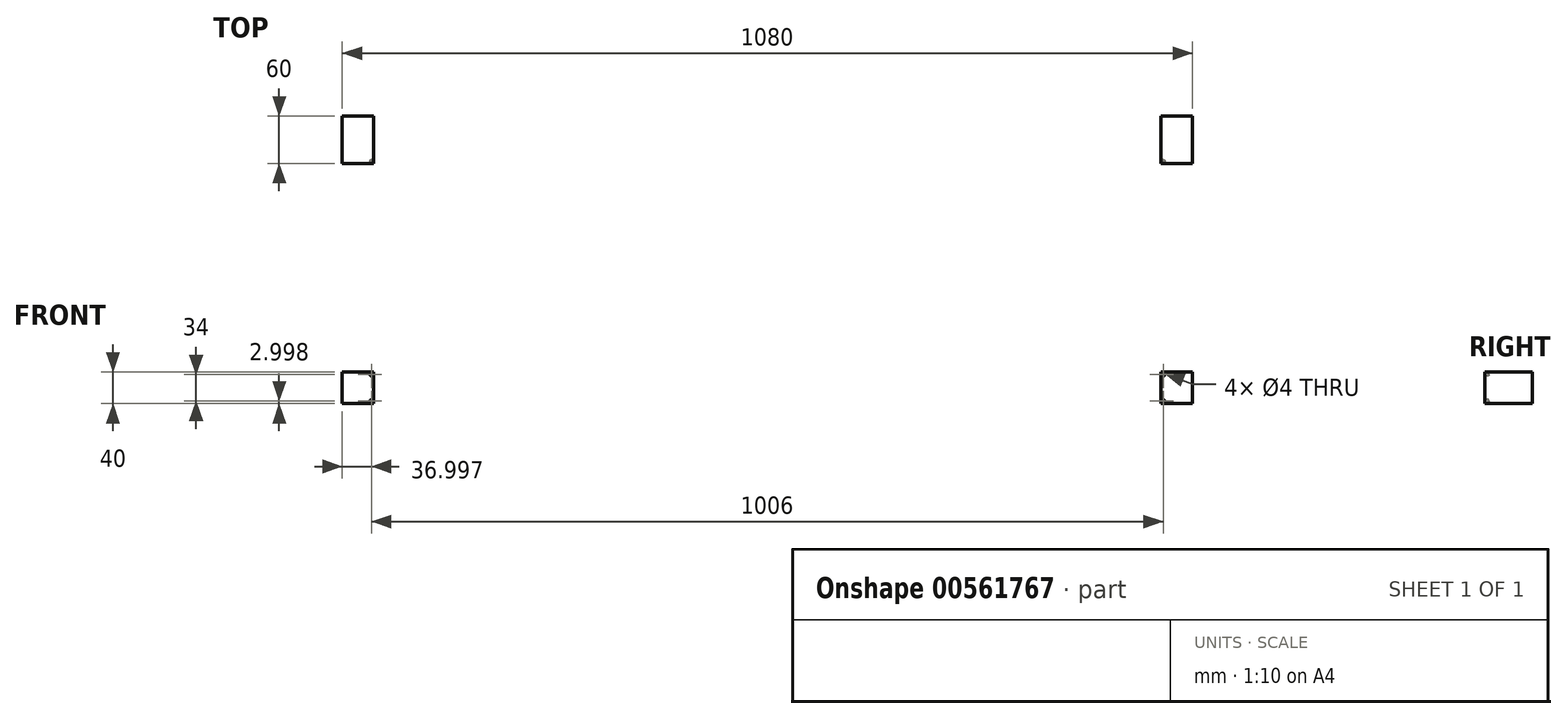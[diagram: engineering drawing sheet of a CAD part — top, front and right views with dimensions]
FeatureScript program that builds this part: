
annotation { "Feature Type Name" : "Feature", "Feature Type Description" : "" }
export const myFeature = defineFeature(function(context is Context, id is Id, definition is map)
    precondition{}
    {
        {
            var Q0;
            Q0=qCreatedBy(makeId("Front.planeOp"),FACE);
            var sketch = newSketch(context, id + "F0", { "sketchPlane" : qUnion([Q0])});
            skLineSegment(sketch, "E0.bottom", {"start": v(-96.02, 22.83) * mm, "end": v(-56.02, 22.83) * mm});
            skLineSegment(sketch, "E0.top", {"start": v(-96.02, -17.17) * mm, "end": v(-56.02, -17.17) * mm});
            skLineSegment(sketch, "E0.left", {"start": v(-96.02, 22.83) * mm, "end": v(-96.02, -17.17) * mm});
            skLineSegment(sketch, "E0.right", {"start": v(-56.02, 22.83) * mm, "end": v(-56.02, -17.17) * mm});
            skLineSegment(sketch, "E1.bottom", {"start": v(943.98, 22.83) * mm, "end": v(983.98, 22.83) * mm});
            skLineSegment(sketch, "E1.top", {"start": v(943.98, -17.17) * mm, "end": v(983.98, -17.17) * mm});
            skLineSegment(sketch, "E1.left", {"start": v(943.98, 22.83) * mm, "end": v(943.98, -17.17) * mm});
            skLineSegment(sketch, "E1.right", {"start": v(983.98, 22.83) * mm, "end": v(983.98, -17.17) * mm});
            skSolve(sketch);
        }
        {
            var Q0;
            Q0 = qSketchRegion(id + "F0", true);
            extrude(context, id + "F1", {"entities" : qUnion([Q0]), "depth" : 60 * mm, "offsetDistance" : 25 * mm});
        }
        {
            var Q0;
            Q0=makeQuery(id+"F1.opExtrude","CAP_FACE",FACE,{"disambiguationData":[OSD([sQuery(id+"F0.wireOp",EDGE,"E1.bottom"),sQuery(id+"F0.wireOp",EDGE,"E1.top"),sQuery(id+"F0.wireOp",EDGE,"E1.left"),sQuery(id+"F0.wireOp",EDGE,"E1.right")])],"isStart":false});
            var sketch = newSketch(context, id + "F2", { "sketchPlane" : qUnion([Q0])});
            skCircle(sketch, "E2", {"center": v(946.98, 19.83) * mm, "radius": 2 * mm});
            skCircle(sketch, "E3.MirrorC", {"center": v(946.98, -14.17) * mm, "radius": 2 * mm});
            skSolve(sketch);
        }
        {
            var Q0;
            Q0=sQuery(id+"F2.wireOp",VERTEX,"E2.center");
            var Q1;
            Q1=sQuery(id+"F2.wireOp",VERTEX,"E3.MirrorC.center");
            var Q2;
            Q2=makeQuery(id+"F1.opExtrude","SWEPT_BODY",BODY,{"disambiguationData":[OSD([sQuery(id+"F0.wireOp",EDGE,"E1.bottom"),sQuery(id+"F0.wireOp",EDGE,"E1.top"),sQuery(id+"F0.wireOp",EDGE,"E1.left"),sQuery(id+"F0.wireOp",EDGE,"E1.right")])]});
            hole(context, id + "F3", {"style" : HoleStyle.SIMPLE, "endStyle" : HoleEndStyle.BLIND, "holeDiameter" : 4 * mm, "majorDiameter" : 5 * mm, "holeDepth" : 4 * mm, "isTappedThrough" : true, "tappedDepth" : 12 * mm, "tapClearance" : 3, "locations" : qUnion([Q0, Q1]), "scope" : qUnion([Q2])});
        }
        {
            var Q0;
            Q0=makeQuery(id+"F1.opExtrude","CAP_FACE",FACE,{"disambiguationData":[OSD([sQuery(id+"F0.wireOp",EDGE,"E0.bottom"),sQuery(id+"F0.wireOp",EDGE,"E0.top"),sQuery(id+"F0.wireOp",EDGE,"E0.left"),sQuery(id+"F0.wireOp",EDGE,"E0.right")])],"isStart":false});
            var sketch = newSketch(context, id + "F4", { "sketchPlane" : qUnion([Q0])});
            skCircle(sketch, "E4", {"center": v(-59.02, 19.83) * mm, "radius": 2 * mm});
            skCircle(sketch, "E5", {"center": v(-59.02, -14.17) * mm, "radius": 2 * mm});
            skSolve(sketch);
        }
        {
            var Q0;
            Q0=sQuery(id+"F4.wireOp",VERTEX,"E4.center");
            var Q1;
            Q1=sQuery(id+"F4.wireOp",VERTEX,"E5.center");
            var Q2;
            Q2=makeQuery(id+"F1.opExtrude","SWEPT_BODY",BODY,{"disambiguationData":[OSD([sQuery(id+"F0.wireOp",EDGE,"E0.bottom"),sQuery(id+"F0.wireOp",EDGE,"E0.top"),sQuery(id+"F0.wireOp",EDGE,"E0.left"),sQuery(id+"F0.wireOp",EDGE,"E0.right")])]});
            hole(context, id + "F5", {"style" : HoleStyle.SIMPLE, "endStyle" : HoleEndStyle.BLIND, "holeDiameter" : 4 * mm, "majorDiameter" : 5 * mm, "holeDepth" : 4 * mm, "isTappedThrough" : true, "tappedDepth" : 12 * mm, "tapClearance" : 3, "locations" : qUnion([Q0, Q1]), "scope" : qUnion([Q2])});
        }
    });
